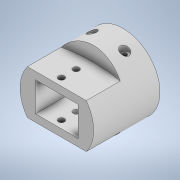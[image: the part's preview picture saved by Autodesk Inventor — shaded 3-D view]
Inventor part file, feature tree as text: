
AUTODESK INVENTOR PART (.ipt)
format: ipt  version: 2022 (Build 260153000, 153)  size: 226,304 bytes
history: native  units: mm
features: extrude x8, sketch x8, mirror x2, plane x1, chamfer x1
ambient origin geometry x8: Origin, YZ Plane, XZ Plane, XY Plane, X Axis, Y Axis, Z Axis, Center Point
bodies: Solid1 (feature_tree)
feature tree (20):
  extrude  "Extrusion1"  Depth=29.0mm
  extrude  "Extrusion2"  Depth=34.5mm
  extrude  "Extrusion4"  Depth=30.0mm TaperAngle=0.0deg
  mirror  "Mirror1"
  extrude  "Extrusion5"  Depth=30.0mm
  plane  "Work Plane1"
  extrude  "Extrusion6"  Depth=75.0mm
  extrude  "Extrusion7"  Depth=25.0mm
  mirror  "Mirror2"
  extrude  "Extrusion9"  Depth=34.5mm
  chamfer  "Chamfer1"  Distance=17.25mm
  extrude  "Extrusion10"  Depth=5.0mm
  sketch  "Sketch1"  dims[d0=50.0mm d1=29.0mm]
  sketch  "Sketch2"  dims[d2=34.5mm d3=14.5mm]
  sketch  "Sketch4"  dims[d4=17.25mm d5=30.0mm d6=0.0mm]
  sketch  "Sketch5"  dims[d7=15.0mm d8=0.0mm d14=30.0mm]
  sketch  "Sketch6"  dims[d15=15.0mm d16=75.0mm]
  sketch  "Sketch7"  dims[d17=25.0mm d18=200.0mm]
  sketch  "Sketch9"  dims[d19=10.0mm d20=0.0mm d21=34.5mm]
  sketch  "Sketch10"  dims[d22=29.0mm d23=17.25mm d24=14.5mm d25=17.0mm d26=0.0mm d27=25.0mm d28=3.0mm d29=3.0mm d30=10.0mm d31=10.0mm d32=22.0mm d33=3.5mm d34=50.0mm d35=0.0mm d36=6.0mm d37=6.0mm d38=5.0mm d39=0.0mm d52=40.0mm d53=0.0mm d57=29.0mm d58=14.5mm d60=7.25mm d61=2.0mm d62=45.0deg d64=5.0mm d65=5.0mm d66=15.0mm d67=5.0mm d68=40.0mm d69=0.0mm]
